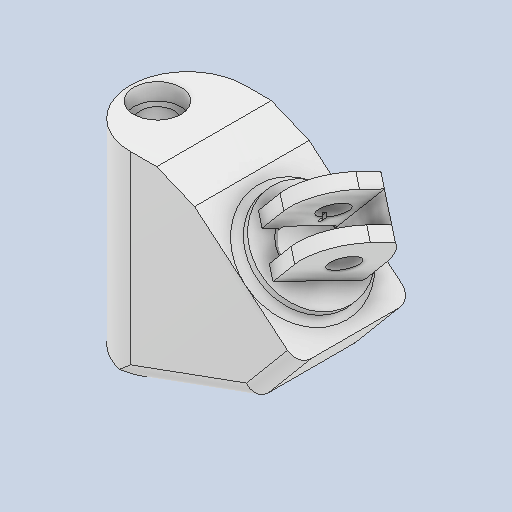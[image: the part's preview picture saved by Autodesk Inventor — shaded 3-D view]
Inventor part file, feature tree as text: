
AUTODESK INVENTOR PART (.ipt)
format: ipt  version: 2022 (Build 260153000, 153)  size: 462,336 bytes
history: native  units: in
note: dims shown in document units (in); Inventor stores cm internally (conversion verified against a paired STEP export)
features: sketch x14, extrude x11, fillet x8, hole x1, plane x1, sweep x1
ambient origin geometry x8: Origin, YZ Plane, XZ Plane, XY Plane, X Axis, Y Axis, Z Axis, Center Point
bodies: Solid1 (feature_tree)
feature tree (36):
  extrude  "Extrusion1"  Depth=0.3937in
  fillet  "Fillet1"  Radius=0.7087in
  extrude  "Extrusion2"  Depth=0.3937in
  fillet  "Fillet2"  [1 undecoded]
  extrude  "Extrusion3"  Depth=0.6693in TaperAngle=0.0deg
  fillet  "Fillet3"  Radius=0.3346in
  extrude  "Extrusion4"  Depth=1.6693in TaperAngle=0.0deg
  fillet  "Fillet4"  Radius=0.0787in
  fillet  "Fillet5"  Radius=0.5906in
  hole  "Hole1"  [1 undecoded]
  sketch  "Sketch7"  dims[d27=0.4331in d28=0.0in d29=0.2362in]
  plane  "Work Plane1"
  sweep  "Sweep1"
  extrude  "Extrusion6"  Depth=0.2362in
  extrude  "Extrusion7"  Depth=0.2953in
  extrude  "Extrusion8"  Depth=0.0394in TaperAngle=0.0deg
  extrude  "Extrusion9"  Depth=0.2756in
  extrude  "Extrusion10"  Depth=0.2756in
  extrude  "Extrusion11"  Depth=0.0197in TaperAngle=0.0deg
  extrude  "Extrusion12"  Depth=0.0197in TaperAngle=0.0deg
  fillet  "Fillet6"  Radius=0.0197in
  fillet  "Fillet7"  Radius=0.0197in
  fillet  "Fillet8"  Radius=0.0197in
  sketch  "Sketch1"  dims[d0=1.1811in d1=0.3937in d2=0.7087in]
  sketch  "Sketch2"  dims[d3=0.1374in d4=0.3937in d5=150.0deg]
  sketch  "Sketch3"  dims[d6=0.7874in d7=0.6693in d8=0.0in d9=0.3346in]
  sketch  "Sketch4"  dims[d12=0.1969in d13=1.6693in d14=0.0in d15=0.0787in d17=0.5906in]
  sketch  "Sketch5"  dims[d18=0.0787in d19=0.0in d20=0.0394in]
  sketch  "Sketch8"  dims[d30=0.3937in d31=0.2362in]
  sketch  "Sketch9"  dims[d32=0.1575in d33=0.2362in d34=0.1575in d35=0.0787in d36=90.0deg d37=0.344in d38=0.8108in d39=0.2953in]
  sketch  "Sketch10"  dims[d42=0.0in d43=0.0in d44=0.0394in d45=0.0in]
  sketch  "Sketch11"  dims[d46=0.0787in d47=0.2756in]
  sketch  "Sketch12"  dims[d48=0.0984in d49=0.0in d50=0.2756in]
  sketch  "Sketch13"  dims[d51=0.0984in d52=0.0in d56=0.0197in d57=0.0in]
  sketch  "Sketch14"  dims[d58=0.0197in d59=0.0in d63=0.0197in d64=0.0in d65=0.0197in d66=0.0in d67=0.0197in d68=0.0197in]
  sketch  "Sketch15"  dims[d69=0.0197in d10=0.0in d11=0.0in d21=0.0344in d40=0.0344in d41=0.0197in]
note: 2 required parameter values undecoded (feature->parameter linkage not recoverable at this tier; creation-order binding heuristic only, values carry confidence <= 0.55)
